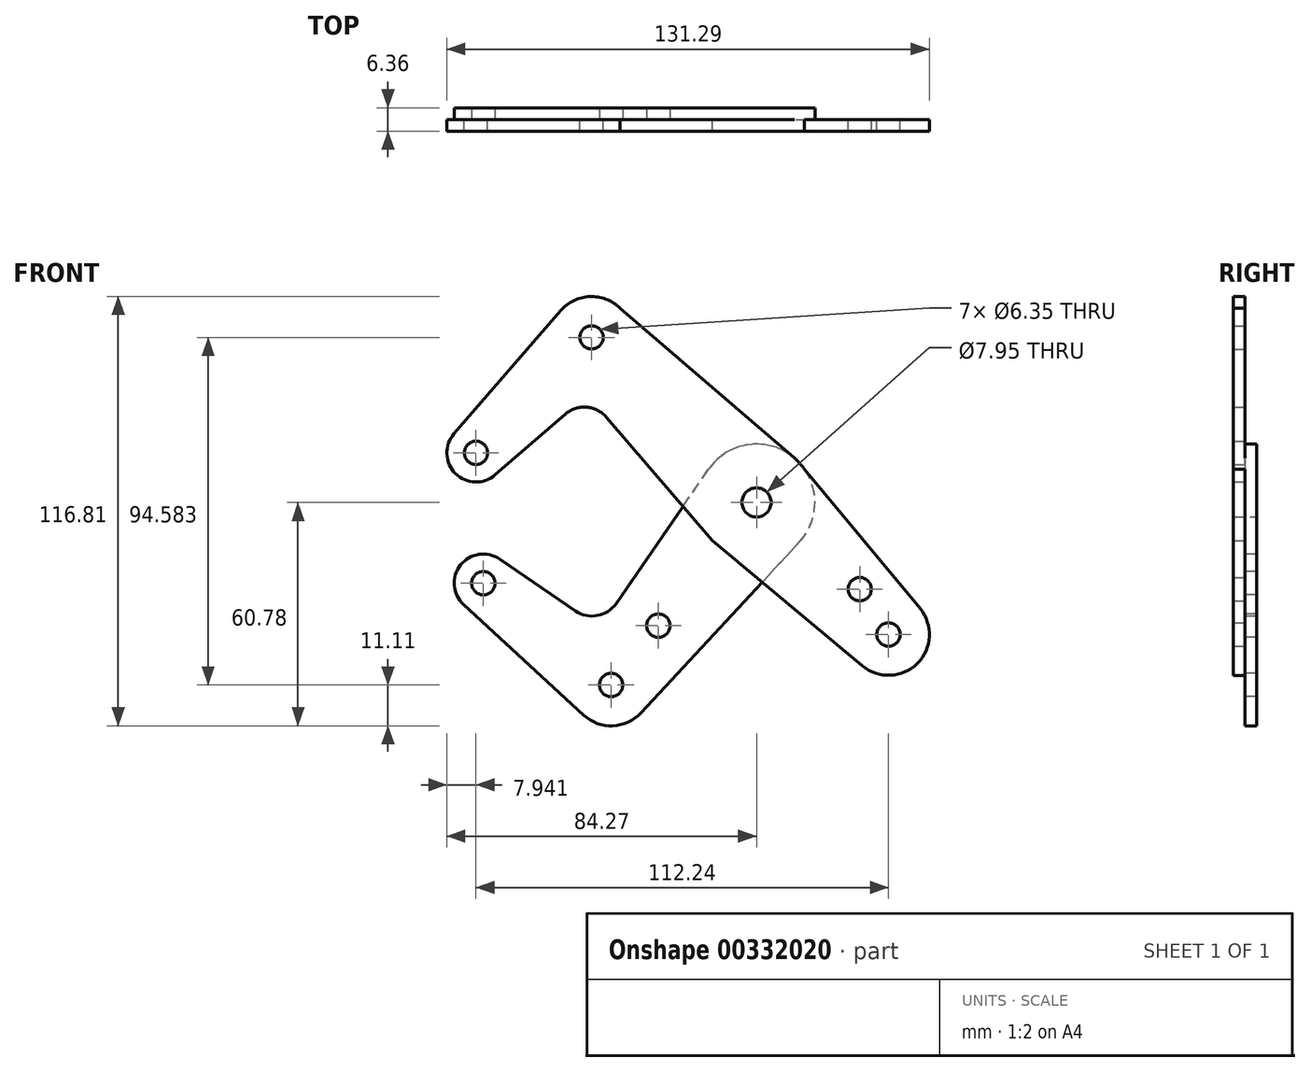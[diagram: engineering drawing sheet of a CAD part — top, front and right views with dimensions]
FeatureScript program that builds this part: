
annotation { "Feature Type Name" : "Feature", "Feature Type Description" : "" }
export const myFeature = defineFeature(function(context is Context, id is Id, definition is map)
    precondition{}
    {
        {
            var Q0;
            Q0=qCreatedBy(makeId("Front.planeOp"),FACE);
            var sketch = newSketch(context, id + "F0", { "sketchPlane" : qUnion([Q0])});
            skCircle(sketch, "E0", {"center": v(0, 0) * mm, "radius": 15.88 * mm});
            skCircle(sketch, "E1", {"center": v(0, 0) * mm, "radius": 3.98 * mm});
            skLineSegment(sketch, "E2", {"start": v(0, 0) * mm, "end": v(-44.89, 44.91) * mm, "construction": true});
            skCircle(sketch, "E3", {"center": v(-44.89, 44.91) * mm, "radius": 11.11 * mm});
            skCircle(sketch, "E4", {"center": v(35.91, -35.93) * mm, "radius": 11.11 * mm});
            skCircle(sketch, "E5", {"center": v(35.91, -35.93) * mm, "radius": 3.18 * mm});
            skCircle(sketch, "E6", {"center": v(-44.89, 44.91) * mm, "radius": 3.18 * mm});
            skLineSegment(sketch, "E7", {"start": v(-44.89, 44.91) * mm, "end": v(-76.33, 13.5) * mm, "construction": true});
            skCircle(sketch, "E8", {"center": v(-76.33, 13.5) * mm, "radius": 7.94 * mm});
            skCircle(sketch, "E9", {"center": v(-76.33, 13.5) * mm, "radius": 3.18 * mm});
            skLineSegment(sketch, "E10", {"start": v(25.82, -25.83) * mm, "end": v(28.07, -23.59) * mm});
            skCircle(sketch, "E11", {"center": v(28.07, -23.59) * mm, "radius": 3.18 * mm});
            skLineSegment(sketch, "E12", {"start": v(0, 0) * mm, "end": v(35.91, -35.93) * mm, "construction": true});
            skLineSegment(sketch, "E13", {"start": v(-82.33, 18.69) * mm, "end": v(-53.29, 52.2) * mm});
            skLineSegment(sketch, "E14", {"start": v(-71.13, 7.49) * mm, "end": v(-52.06, 24) * mm});
            skLineSegment(sketch, "E15", {"start": v(-37.15, 52.9) * mm, "end": v(10.35, 12.04) * mm});
            skLineSegment(sketch, "E16", {"start": v(-40.83, 23.17) * mm, "end": v(-12.04, -10.34) * mm});
            skArc(sketch, "E17.filletArc", {"start": v(-40.83, 23.17) * mm, "mid": v(-46.27, 25.92) * mm, "end": v(-52.06, 24) * mm});
            skLineSegment(sketch, "E18", {"start": v(-12.04, -10.34) * mm, "end": v(28.79, -44.46) * mm});
            skLineSegment(sketch, "E19", {"start": v(13.05, 9.04) * mm, "end": v(44.46, -28.84) * mm});
            skSolve(sketch);
        }
        {
            var Q0;
            {var subQ0=sQuery(id+"F0.wireOp",EDGE,"E13");Q0=makeQuery(id+"F0.imprint","IMPRINT",FACE,{"disambiguationData":[TD([[makeQuery(id+"F0.imprint","IMPRINT",EDGE,{"derivedFrom":subQ0}),-1.0]])]});}
            var Q1;
            Q1=makeQuery(id+"F0.imprint","IMPRINT",FACE,{"disambiguationData":[TD([[makeQuery(id+"F0.imprint","IMPRINT",EDGE,{"derivedFrom":sQuery(id+"F0.wireOp",EDGE,"E6")}),-1.0]])]});
            var Q2;
            Q2=makeQuery(id+"F0.imprint","IMPRINT",FACE,{"disambiguationData":[TD([[makeQuery(id+"F0.imprint","IMPRINT",EDGE,{"derivedFrom":sQuery(id+"F0.wireOp",EDGE,"E9")}),-1.0]])]});
            var Q3;
            Q3=makeQuery(id+"F0.imprint","IMPRINT",FACE,{"disambiguationData":[TD([[makeQuery(id+"F0.imprint","IMPRINT",EDGE,{"derivedFrom":sQuery(id+"F0.wireOp",EDGE,"E1")}),-1.0]])]});
            var Q4;
            Q4=makeQuery(id+"F0.imprint","IMPRINT",FACE,{"disambiguationData":[TD([[makeQuery(id+"F0.imprint","IMPRINT",EDGE,{"derivedFrom":sQuery(id+"F0.wireOp",EDGE,"E11")}),-1.0]])]});
            var Q5;
            Q5=makeQuery(id+"F0.imprint","IMPRINT",FACE,{"disambiguationData":[TD([[makeQuery(id+"F0.imprint","IMPRINT",EDGE,{"derivedFrom":sQuery(id+"F0.wireOp",EDGE,"E5")}),-1.0]])]});
            extrude(context, id + "F1", {"entities" : qUnion([Q0, Q1, Q2, Q3, Q4, Q5]), "depth" : 3.17 * mm});
        }
        {
            var Q0;
            Q0=qCreatedBy(makeId("Front.planeOp"),FACE);
            var sketch = newSketch(context, id + "F2", { "sketchPlane" : qUnion([Q0])});
            skCircle(sketch, "E20", {"center": v(0, 0) * mm, "radius": 15.88 * mm});
            skLineSegment(sketch, "E21", {"start": v(0, 0) * mm, "end": v(-39.56, -49.67) * mm, "construction": true});
            skCircle(sketch, "E22", {"center": v(-39.56, -49.67) * mm, "radius": 11.11 * mm});
            skLineSegment(sketch, "E23", {"start": v(-39.56, -49.67) * mm, "end": v(-74.33, -21.98) * mm, "construction": true});
            skCircle(sketch, "E24", {"center": v(-74.33, -21.98) * mm, "radius": 7.94 * mm});
            skCircle(sketch, "E25", {"center": v(-74.33, -21.98) * mm, "radius": 3.18 * mm});
            skCircle(sketch, "E26", {"center": v(-39.56, -49.67) * mm, "radius": 3.17 * mm});
            skLineSegment(sketch, "E27", {"start": v(-39.56, -49.67) * mm, "end": v(-26.7, -33.52) * mm});
            skCircle(sketch, "E28", {"center": v(-26.7, -33.52) * mm, "radius": 3.18 * mm});
            skLineSegment(sketch, "E29", {"start": v(-79.7, -27.82) * mm, "end": v(-47.09, -57.85) * mm});
            skLineSegment(sketch, "E30", {"start": v(-38.23, -27.47) * mm, "end": v(-13.07, 9.01) * mm});
            skLineSegment(sketch, "E31", {"start": v(-31.41, -57.23) * mm, "end": v(11.64, -10.8) * mm});
            skArc(sketch, "E32.filletArc", {"start": v(-49.28, -29.51) * mm, "mid": v(-43.33, -30.77) * mm, "end": v(-38.23, -27.47) * mm});
            skLineSegment(sketch, "E33", {"start": v(-49.28, -29.51) * mm, "end": v(-69.85, -15.43) * mm});
            skCircle(sketch, "E34", {"center": v(0, 0) * mm, "radius": 3.98 * mm});
            skSolve(sketch);
        }
        {
            var Q0;
            Q0=makeQuery(id+"F2.imprint","IMPRINT",FACE,{"disambiguationData":[TD([[makeQuery(id+"F2.imprint","IMPRINT",EDGE,{"derivedFrom":sQuery(id+"F2.wireOp",EDGE,"E28")}),-1.0]])]});
            var Q1;
            Q1=makeQuery(id+"F2.imprint","IMPRINT",FACE,{"disambiguationData":[TD([[makeQuery(id+"F2.imprint","IMPRINT",EDGE,{"derivedFrom":sQuery(id+"F2.wireOp",EDGE,"E25")}),-1.0]])]});
            var Q2;
            Q2=makeQuery(id+"F2.imprint","IMPRINT",FACE,{"disambiguationData":[TD([[makeQuery(id+"F2.imprint","IMPRINT",EDGE,{"derivedFrom":sQuery(id+"F2.wireOp",EDGE,"E34")}),-1.0]])]});
            var Q3;
            Q3=makeQuery(id+"F2.imprint","IMPRINT",FACE,{"disambiguationData":[TD([[makeQuery(id+"F2.imprint","IMPRINT",EDGE,{"derivedFrom":sQuery(id+"F2.wireOp",EDGE,"E26")}),-1.0]])]});
            extrude(context, id + "F3", {"entities" : qUnion([Q0, Q1, Q2, Q3]), "operationType" : NewBodyOperationType.ADD, "oppositeDirection" : true, "depth" : 3.17 * mm});
        }
    });
